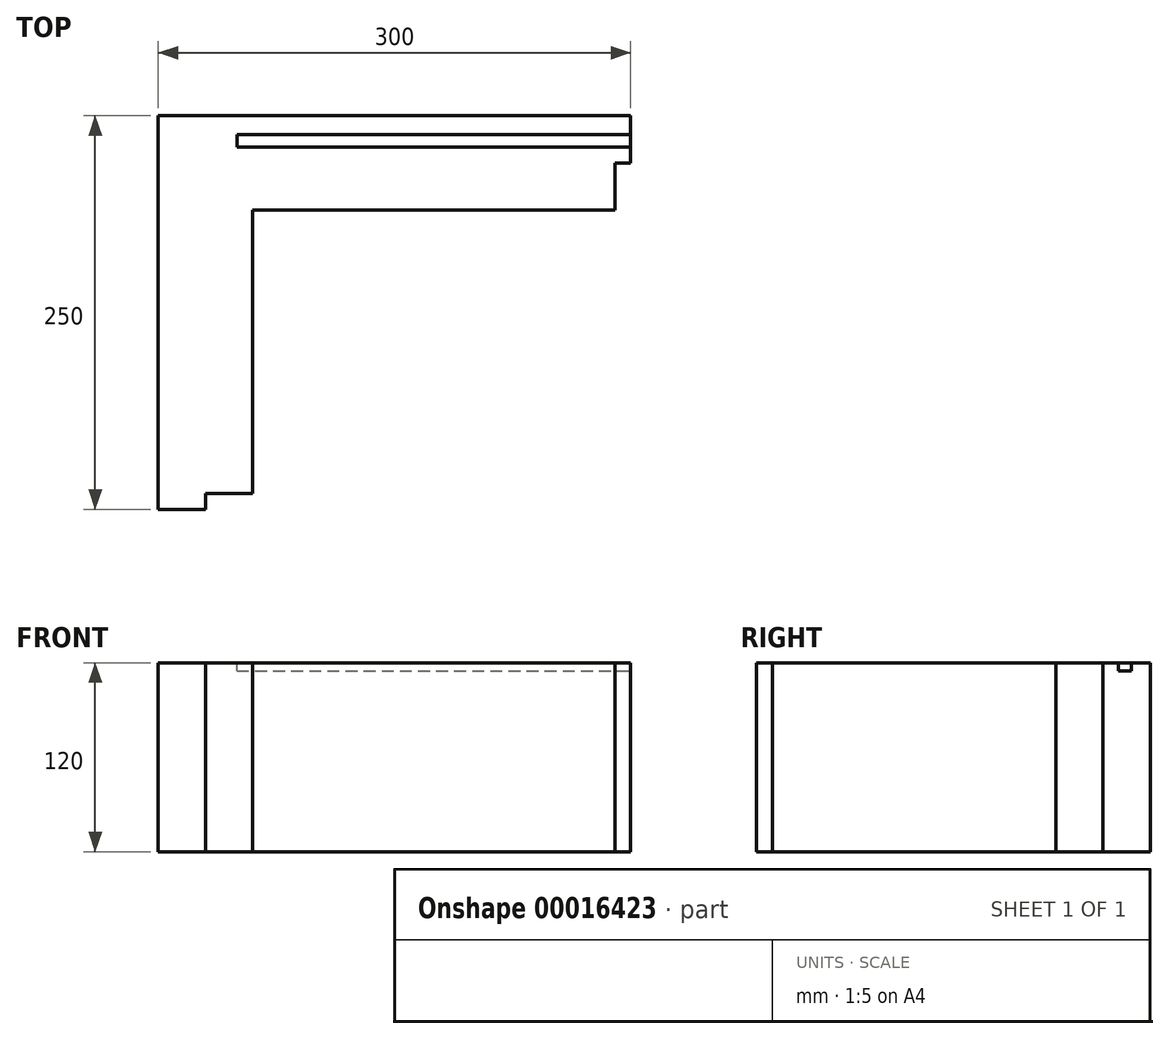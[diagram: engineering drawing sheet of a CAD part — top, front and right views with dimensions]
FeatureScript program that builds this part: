
annotation { "Feature Type Name" : "Feature", "Feature Type Description" : "" }
export const myFeature = defineFeature(function(context is Context, id is Id, definition is map)
    precondition{}
    {
        {
            var Q0;
            Q0=qCreatedBy(makeId("Top.planeOp"),FACE);
            var sketch = newSketch(context, id + "F0", { "sketchPlane" : qUnion([Q0])});
            skLineSegment(sketch, "E0.bottom", {"start": v(0, 0) * mm, "end": v(30, 0) * mm});
            skLineSegment(sketch, "E0.top", {"start": v(0, 250) * mm, "end": v(60, 250) * mm});
            skLineSegment(sketch, "E0.left", {"start": v(0, 0) * mm, "end": v(0, 250) * mm});
            skLineSegment(sketch, "E0.right", {"start": v(60, 0) * mm, "end": v(60, 220) * mm});
            skLineSegment(sketch, "E1.bottom", {"start": v(60, 250) * mm, "end": v(290, 250) * mm});
            skLineSegment(sketch, "E1.top", {"start": v(60, 190) * mm, "end": v(290, 190) * mm});
            skLineSegment(sketch, "E1.left", {"start": v(60, 220) * mm, "end": v(60, 190) * mm});
            skLineSegment(sketch, "E1.right", {"start": v(290, 220) * mm, "end": v(290, 190) * mm});
            skLineSegment(sketch, "E2.bottom", {"start": v(290, 250) * mm, "end": v(350, 250) * mm});
            skLineSegment(sketch, "E2.top", {"start": v(320, 0) * mm, "end": v(350, 0) * mm});
            skLineSegment(sketch, "E2.left", {"start": v(290, 220) * mm, "end": v(290, 0) * mm});
            skLineSegment(sketch, "E2.right", {"start": v(350, 250) * mm, "end": v(350, 0) * mm});
            skLineSegment(sketch, "E3.bottom", {"start": v(60, 250) * mm, "end": v(50, 250) * mm});
            skLineSegment(sketch, "E3.top", {"start": v(60, 220) * mm, "end": v(50, 220) * mm});
            skLineSegment(sketch, "E3.right", {"start": v(50, 250) * mm, "end": v(50, 220) * mm});
            skLineSegment(sketch, "E4.bottom", {"start": v(290, 250) * mm, "end": v(300, 250) * mm});
            skLineSegment(sketch, "E4.top", {"start": v(290, 220) * mm, "end": v(300, 220) * mm});
            skLineSegment(sketch, "E4.right", {"start": v(300, 250) * mm, "end": v(300, 220) * mm});
            skLineSegment(sketch, "E5.top", {"start": v(0, -110) * mm, "end": v(60, -110) * mm});
            skLineSegment(sketch, "E5.left", {"start": v(0, 0) * mm, "end": v(0, -110) * mm});
            skLineSegment(sketch, "E5.right", {"start": v(60, 0) * mm, "end": v(60, -110) * mm});
            skLineSegment(sketch, "E6.bottom", {"start": v(320, 0) * mm, "end": v(350.17, 0) * mm});
            skLineSegment(sketch, "E6.top", {"start": v(290, -110) * mm, "end": v(350.17, -110) * mm});
            skLineSegment(sketch, "E6.left", {"start": v(290, 0) * mm, "end": v(290, -110) * mm});
            skLineSegment(sketch, "E6.right", {"start": v(350.17, 0) * mm, "end": v(350.17, -110) * mm});
            skLineSegment(sketch, "E7.top", {"start": v(60, 10) * mm, "end": v(30, 10) * mm});
            skLineSegment(sketch, "E7.left", {"start": v(60, 0) * mm, "end": v(60, 10) * mm});
            skLineSegment(sketch, "E7.right", {"start": v(30, 0) * mm, "end": v(30, 10) * mm});
            skLineSegment(sketch, "E8.top", {"start": v(290, 10) * mm, "end": v(320, 10) * mm});
            skLineSegment(sketch, "E8.left", {"start": v(290, 0) * mm, "end": v(290, 10) * mm});
            skLineSegment(sketch, "E8.right", {"start": v(320, 0) * mm, "end": v(320, 10) * mm});
            skSolve(sketch);
        }
        {
            var Q0;
            Q0=makeQuery(id+"F0.imprint","IMPRINT",FACE,{"disambiguationData":[TD([[makeQuery(id+"F0.imprint","IMPRINT",EDGE,{"derivedFrom":sQuery(id+"F0.wireOp",EDGE,"E1.bottom")}),-1.0]])]});
            extrude(context, id + "F1", {"entities" : qUnion([Q0]), "depth" : 120 * mm});
        }
        {
            var Q0;
            Q0=makeQuery(id+"F0.imprint","IMPRINT",FACE,{"disambiguationData":[TD([[makeQuery(id+"F0.imprint","IMPRINT",EDGE,{"derivedFrom":sQuery(id+"F0.wireOp",EDGE,"E0.top")}),-1.0]])]});
            extrude(context, id + "F2", {"entities" : qUnion([Q0]), "operationType" : NewBodyOperationType.ADD, "depth" : 120 * mm});
        }
        {
            var Q0;
            Q0=makeQuery(id+"F1.opExtrude","CAP_FACE",FACE,{"disambiguationData":[OSD([sQuery(id+"F0.wireOp",EDGE,"E1.bottom"),sQuery(id+"F0.wireOp",EDGE,"E1.top"),sQuery(id+"F0.wireOp",EDGE,"E1.left"),sQuery(id+"F0.wireOp",EDGE,"E2.left"),sQuery(id+"F0.wireOp",EDGE,"E3.bottom"),sQuery(id+"F0.wireOp",EDGE,"E3.top"),sQuery(id+"F0.wireOp",EDGE,"E3.right"),sQuery(id+"F0.wireOp",EDGE,"E4.bottom"),sQuery(id+"F0.wireOp",EDGE,"E4.top"),sQuery(id+"F0.wireOp",EDGE,"E4.right")])],"isStart":false});
            var sketch = newSketch(context, id + "F3", { "sketchPlane" : qUnion([Q0])});
            skLineSegment(sketch, "E9.bottom", {"start": v(50, 238) * mm, "end": v(300, 238) * mm});
            skLineSegment(sketch, "E9.top", {"start": v(50, 230) * mm, "end": v(300, 230) * mm});
            skLineSegment(sketch, "E9.left", {"start": v(50, 238) * mm, "end": v(50, 230) * mm});
            skLineSegment(sketch, "E9.right", {"start": v(300, 238) * mm, "end": v(300, 230) * mm});
            skSolve(sketch);
        }
        {
            var Q0;
            Q0=makeQuery(id+"F3.imprint","IMPRINT",FACE,{"disambiguationData":[TD([[makeQuery(id+"F3.imprint","IMPRINT",EDGE,{"derivedFrom":sQuery(id+"F3.wireOp",EDGE,"E9.bottom")}),-1.0]])]});
            extrude(context, id + "F4", {"entities" : qUnion([Q0]), "operationType" : NewBodyOperationType.REMOVE, "oppositeDirection" : true, "depth" : 5 * mm});
        }
    });
